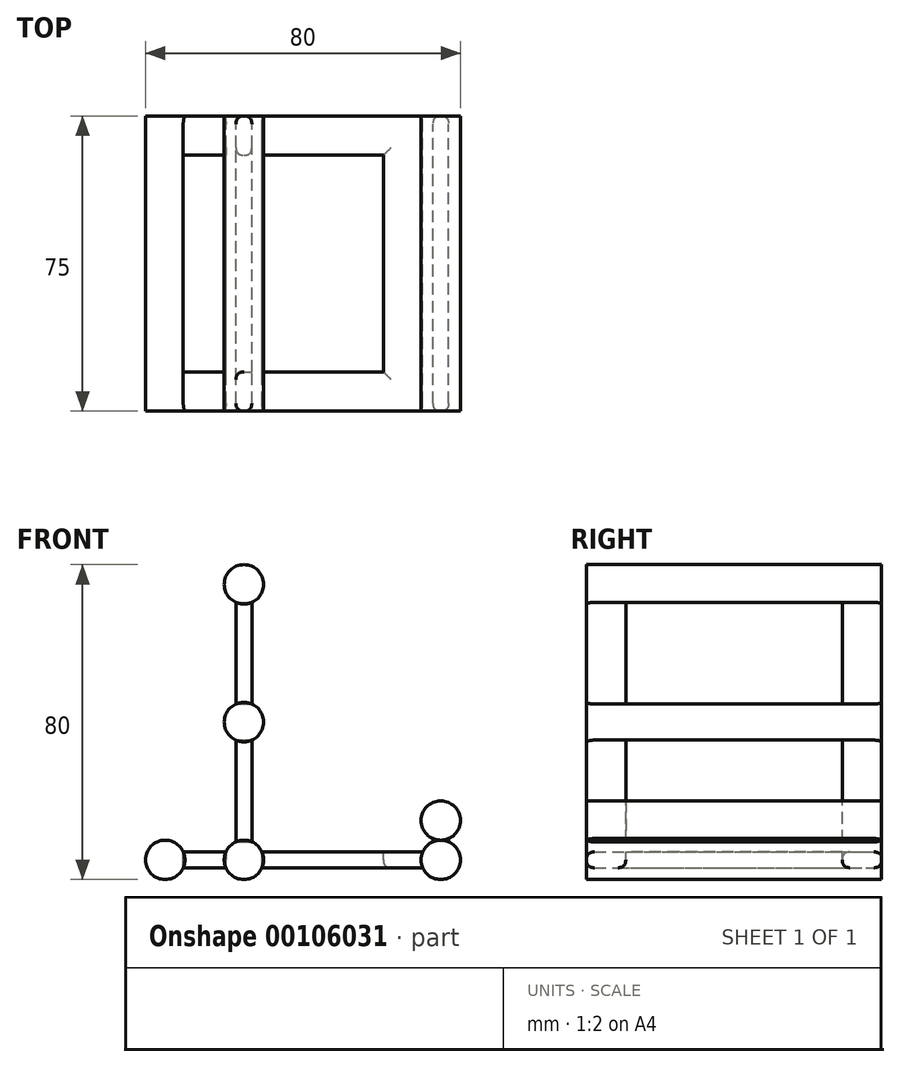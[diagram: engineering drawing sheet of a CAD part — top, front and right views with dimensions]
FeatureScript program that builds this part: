
annotation { "Feature Type Name" : "Feature", "Feature Type Description" : "" }
export const myFeature = defineFeature(function(context is Context, id is Id, definition is map)
    precondition{}
    {
        {
            var Q0;
            Q0=qCreatedBy(makeId("Front.planeOp"),FACE);
            var sketch = newSketch(context, id + "F0", { "sketchPlane" : qUnion([Q0])});
            skArc(sketch, "E0", {"start": v(3, 9.58) * mm, "mid": v(1.46, 8.54) * mm, "end": v(0.42, 7) * mm});
            skArc(sketch, "E1", {"start": v(50.42, 3) * mm, "mid": v(58.54, 1.46) * mm, "end": v(57, 9.58) * mm});
            skArc(sketch, "E2", {"start": v(7, 70.42) * mm, "mid": v(5, 80) * mm, "end": v(3, 70.42) * mm});
            skArc(sketch, "E3", {"start": v(3, 44.58) * mm, "mid": v(0, 40) * mm, "end": v(3, 35.42) * mm});
            skLineSegment(sketch, "E4.top", {"start": v(7, 5) * mm, "end": v(5, 5) * mm});
            skLineSegment(sketch, "E4.left", {"start": v(7, 70.42) * mm, "end": v(7, 44.58) * mm});
            skLineSegment(sketch, "E4.right", {"start": v(3, 70.42) * mm, "end": v(3, 44.58) * mm});
            skLineSegment(sketch, "E5.bottom", {"start": v(50.42, 7) * mm, "end": v(9.58, 7) * mm});
            skLineSegment(sketch, "E5.top", {"start": v(50.42, 3) * mm, "end": v(9.58, 3) * mm});
            skLineSegment(sketch, "E5.right", {"start": v(5, 7) * mm, "end": v(5, 5) * mm});
            skPoint(sketch, "E5.middle", {"position": v(30, 5) * mm});
            skPoint(sketch, "E6.orphan", {"position": v(7, 75) * mm});
            skPoint(sketch, "E7.orphan", {"position": v(3, 75) * mm});
            skLineSegment(sketch, "E8.trimOffspring", {"start": v(7, 35.42) * mm, "end": v(7, 9.58) * mm});
            skLineSegment(sketch, "E9.trimOffspring", {"start": v(3, 35.42) * mm, "end": v(3, 9.58) * mm});
            skArc(sketch, "E10.trimOffspring", {"start": v(7, 35.42) * mm, "mid": v(10, 40) * mm, "end": v(7, 44.58) * mm});
            skPoint(sketch, "E11.orphan", {"position": v(3, 5) * mm});
            skPoint(sketch, "E12.orphan", {"position": v(5, 3) * mm});
            skArc(sketch, "E13.trimOffspring", {"start": v(9.58, 7) * mm, "mid": v(8.54, 8.54) * mm, "end": v(7, 9.58) * mm});
            skPoint(sketch, "E5.left.start.orphan", {"position": v(55, 7) * mm});
            skPoint(sketch, "E14.orphan", {"position": v(55, 3) * mm});
            skArc(sketch, "E15", {"start": v(57, 10.42) * mm, "mid": v(55, 20) * mm, "end": v(53, 10.42) * mm});
            skLineSegment(sketch, "E16.left", {"start": v(57, 10.42) * mm, "end": v(57, 9.58) * mm});
            skLineSegment(sketch, "E16.right", {"start": v(53, 10.42) * mm, "end": v(53, 9.58) * mm});
            skPoint(sketch, "E16.middle", {"position": v(55, 10) * mm});
            skArc(sketch, "E17.trimOffspring", {"start": v(53, 9.58) * mm, "mid": v(51.46, 8.54) * mm, "end": v(50.42, 7) * mm});
            skPoint(sketch, "E18.orphan", {"position": v(57, 15) * mm});
            skPoint(sketch, "E19.orphan", {"position": v(53, 15) * mm});
            skPoint(sketch, "E20.orphan", {"position": v(53, 5) * mm});
            skPoint(sketch, "E21.orphan", {"position": v(57, 5) * mm});
            skArc(sketch, "E22", {"start": v(-10.42, 7) * mm, "mid": v(-20, 5) * mm, "end": v(-10.42, 3) * mm});
            skLineSegment(sketch, "E23", {"start": v(9.58, 7) * mm, "end": v(5, 7) * mm});
            skLineSegment(sketch, "E24", {"start": v(9.58, 3) * mm, "end": v(5, 3) * mm});
            skArc(sketch, "E25.trimOffspring", {"start": v(0.42, 3) * mm, "mid": v(5, 0) * mm, "end": v(9.58, 3) * mm});
            skLineSegment(sketch, "E26.trimOffspring", {"start": v(0.42, 7) * mm, "end": v(-10.42, 7) * mm});
            skLineSegment(sketch, "E27.trimOffspring", {"start": v(0.42, 3) * mm, "end": v(-10.42, 3) * mm});
            skSolve(sketch);
        }
        {
            var Q0;
            Q0=makeQuery(id+"F0.imprint","IMPRINT",FACE,{"disambiguationData":[TD([[makeQuery(id+"F0.imprint","IMPRINT",EDGE,{"derivedFrom":sQuery(id+"F0.wireOp",EDGE,"E0")}),1.0]])]});
            extrude(context, id + "F1", {"entities" : qUnion([Q0]), "depth" : 75 * mm});
        }
        {
            var Q0;
            Q0=makeQuery(id+"F1.opExtrude","SWEPT_FACE",FACE,{"disambiguationData":[OSD([sQuery(id+"F0.wireOp",EDGE,"E4.left")])]});
            var sketch = newSketch(context, id + "F2", { "sketchPlane" : qUnion([Q0])});
            skLineSegment(sketch, "E28.bottom", {"start": v(-65, 70.42) * mm, "end": v(-10, 70.42) * mm});
            skLineSegment(sketch, "E28.top", {"start": v(-65, 44.58) * mm, "end": v(-10, 44.58) * mm});
            skLineSegment(sketch, "E28.left", {"start": v(-65, 70.42) * mm, "end": v(-65, 44.58) * mm});
            skLineSegment(sketch, "E28.right", {"start": v(-10, 70.42) * mm, "end": v(-10, 44.58) * mm});
            skSolve(sketch);
        }
        {
            var Q0;
            Q0=makeQuery(id+"F1.opExtrude","SWEPT_FACE",FACE,{"disambiguationData":[OSD([sQuery(id+"F0.wireOp",EDGE,"E8.trimOffspring")])]});
            var sketch = newSketch(context, id + "F3", { "sketchPlane" : qUnion([Q0])});
            skLineSegment(sketch, "E29.bottom", {"start": v(-65, 35.42) * mm, "end": v(-10, 35.42) * mm});
            skLineSegment(sketch, "E29.top", {"start": v(-65, 9.58) * mm, "end": v(-10, 9.58) * mm});
            skLineSegment(sketch, "E29.left", {"start": v(-65, 35.42) * mm, "end": v(-65, 9.58) * mm});
            skLineSegment(sketch, "E29.right", {"start": v(-10, 35.42) * mm, "end": v(-10, 9.58) * mm});
            skSolve(sketch);
        }
        {
            var Q0;
            Q0=makeQuery(id+"F1.opExtrude","SWEPT_FACE",FACE,{"disambiguationData":[OSD([sQuery(id+"F0.wireOp",EDGE,"E5.bottom")])]});
            var sketch = newSketch(context, id + "F4", { "sketchPlane" : qUnion([Q0])});
            skLineSegment(sketch, "E30.bottom", {"start": v(9.58, -10) * mm, "end": v(40.42, -10) * mm});
            skLineSegment(sketch, "E30.top", {"start": v(9.58, -65) * mm, "end": v(40.42, -65) * mm});
            skLineSegment(sketch, "E30.left", {"start": v(9.58, -10) * mm, "end": v(9.58, -65) * mm});
            skLineSegment(sketch, "E30.right", {"start": v(40.42, -10) * mm, "end": v(40.42, -65) * mm});
            skSolve(sketch);
        }
        {
            var Q0;
            Q0=makeQuery(id+"F2.imprint","IMPRINT",FACE,{"disambiguationData":[TD([[makeQuery(id+"F2.imprint","IMPRINT",EDGE,{"derivedFrom":sQuery(id+"F2.wireOp",EDGE,"E28.bottom")}),-1.0]])]});
            extrude(context, id + "F5", {"entities" : qUnion([Q0]), "operationType" : NewBodyOperationType.REMOVE, "oppositeDirection" : true, "depth" : 5 * mm});
        }
        {
            var Q0;
            Q0=makeQuery(id+"F3.imprint","IMPRINT",FACE,{"disambiguationData":[TD([[makeQuery(id+"F3.imprint","IMPRINT",EDGE,{"derivedFrom":sQuery(id+"F3.wireOp",EDGE,"E29.bottom")}),-1.0]])]});
            extrude(context, id + "F6", {"entities" : qUnion([Q0]), "operationType" : NewBodyOperationType.REMOVE, "oppositeDirection" : true, "depth" : 5 * mm});
        }
        {
            var Q0;
            Q0=makeQuery(id+"F4.imprint","IMPRINT",FACE,{"disambiguationData":[TD([[makeQuery(id+"F4.imprint","IMPRINT",EDGE,{"derivedFrom":sQuery(id+"F4.wireOp",EDGE,"E30.bottom")}),-1.0]])]});
            extrude(context, id + "F7", {"entities" : qUnion([Q0]), "operationType" : NewBodyOperationType.REMOVE, "oppositeDirection" : true, "depth" : 5 * mm});
        }
        {
            var Q0;
            Q0=makeQuery(id+"F1.opExtrude","SWEPT_FACE",FACE,{"disambiguationData":[OSD([sQuery(id+"F0.wireOp",EDGE,"E26.trimOffspring")])]});
            var sketch = newSketch(context, id + "F8", { "sketchPlane" : qUnion([Q0])});
            skLineSegment(sketch, "E31.bottom", {"start": v(0.42, -10) * mm, "end": v(-10.42, -10) * mm});
            skLineSegment(sketch, "E31.top", {"start": v(0.42, -65) * mm, "end": v(-10.42, -65) * mm});
            skLineSegment(sketch, "E31.left", {"start": v(0.42, -10) * mm, "end": v(0.42, -65) * mm});
            skLineSegment(sketch, "E31.right", {"start": v(-10.42, -10) * mm, "end": v(-10.42, -65) * mm});
            skSolve(sketch);
        }
        {
            var Q0;
            Q0=makeQuery(id+"F8.imprint","IMPRINT",FACE,{"disambiguationData":[TD([[makeQuery(id+"F8.imprint","IMPRINT",EDGE,{"derivedFrom":sQuery(id+"F8.wireOp",EDGE,"E31.bottom")}),1.0]])]});
            extrude(context, id + "F9", {"entities" : qUnion([Q0]), "operationType" : NewBodyOperationType.REMOVE, "oppositeDirection" : true, "depth" : 5 * mm});
        }
        {
            var Q0;
            Q0=makeQuery(id+"F1.opExtrude","CAP_EDGE",EDGE,{"disambiguationData":[OSD([sQuery(id+"F0.wireOp",EDGE,"E27.trimOffspring")])],"isStart":false});
            var Q1;
            Q1=makeQuery(id+"F9.boolean.opBoolean","INTERSECT",EDGE,{"derivedFrom":[makeQuery(id+"F1.opExtrude","SWEPT_FACE",FACE,{"disambiguationData":[OSD([sQuery(id+"F0.wireOp",EDGE,"E27.trimOffspring")])]}),makeQuery(id+"F9.opExtrude","SWEPT_FACE",FACE,{"disambiguationData":[OSD([sQuery(id+"F8.wireOp",EDGE,"E31.bottom")])]})]});
            var Q2;
            Q2=makeQuery(id+"F1.opExtrude","CAP_EDGE",EDGE,{"disambiguationData":[OSD([sQuery(id+"F0.wireOp",EDGE,"E27.trimOffspring")])],"isStart":true});
            var Q3;
            Q3=makeQuery(id+"F1.opExtrude","CAP_EDGE",EDGE,{"disambiguationData":[OSD([sQuery(id+"F0.wireOp",EDGE,"E5.top")])],"isStart":false});
            var Q4;
            Q4=makeQuery(id+"F7.boolean.opBoolean","INTERSECT",EDGE,{"derivedFrom":[makeQuery(id+"F1.opExtrude","SWEPT_FACE",FACE,{"disambiguationData":[OSD([sQuery(id+"F0.wireOp",EDGE,"E5.top")])]}),makeQuery(id+"F7.opExtrude","SWEPT_FACE",FACE,{"disambiguationData":[OSD([sQuery(id+"F4.wireOp",EDGE,"E30.top")])]})]});
            var Q5;
            Q5=makeQuery(id+"F7.boolean.opBoolean","INTERSECT",EDGE,{"derivedFrom":[makeQuery(id+"F1.opExtrude","SWEPT_FACE",FACE,{"disambiguationData":[OSD([sQuery(id+"F0.wireOp",EDGE,"E5.top")])]}),makeQuery(id+"F7.opExtrude","SWEPT_FACE",FACE,{"disambiguationData":[OSD([sQuery(id+"F4.wireOp",EDGE,"E30.right")])]})]});
            var Q6;
            Q6=makeQuery(id+"F7.boolean.opBoolean","INTERSECT",EDGE,{"derivedFrom":[makeQuery(id+"F1.opExtrude","SWEPT_FACE",FACE,{"disambiguationData":[OSD([sQuery(id+"F0.wireOp",EDGE,"E5.top")])]}),makeQuery(id+"F7.opExtrude","SWEPT_FACE",FACE,{"disambiguationData":[OSD([sQuery(id+"F4.wireOp",EDGE,"E30.bottom")])]})]});
            var Q7;
            Q7=makeQuery(id+"F1.opExtrude","CAP_EDGE",EDGE,{"disambiguationData":[OSD([sQuery(id+"F0.wireOp",EDGE,"E5.top")])],"isStart":true});
            var Q8;
            Q8=makeQuery(id+"F9.boolean.opBoolean","INTERSECT",EDGE,{"derivedFrom":[makeQuery(id+"F1.opExtrude","SWEPT_FACE",FACE,{"disambiguationData":[OSD([sQuery(id+"F0.wireOp",EDGE,"E27.trimOffspring")])]}),makeQuery(id+"F9.opExtrude","SWEPT_FACE",FACE,{"disambiguationData":[OSD([sQuery(id+"F8.wireOp",EDGE,"E31.top")])]})]});
            var Q9;
            Q9=makeQuery(id+"F1.opExtrude","CAP_EDGE",EDGE,{"disambiguationData":[OSD([sQuery(id+"F0.wireOp",EDGE,"E26.trimOffspring")])],"isStart":false});
            var Q10;
            Q10=makeQuery(id+"F9.boolean.opBoolean","COPY",EDGE,{"derivedFrom":makeQuery(id+"F9.opExtrude","CAP_EDGE",EDGE,{"disambiguationData":[OSD([sQuery(id+"F8.wireOp",EDGE,"E31.top")])],"isStart":true})});
            var Q11;
            Q11=makeQuery(id+"F1.opExtrude","CAP_EDGE",EDGE,{"disambiguationData":[OSD([sQuery(id+"F0.wireOp",EDGE,"E5.bottom")])],"isStart":false});
            var Q12;
            Q12=makeQuery(id+"F7.boolean.opBoolean","COPY",EDGE,{"derivedFrom":makeQuery(id+"F7.opExtrude","CAP_EDGE",EDGE,{"disambiguationData":[OSD([sQuery(id+"F4.wireOp",EDGE,"E30.top")])],"isStart":true})});
            var Q13;
            Q13=makeQuery(id+"F9.boolean.opBoolean","COPY",EDGE,{"derivedFrom":makeQuery(id+"F9.opExtrude","CAP_EDGE",EDGE,{"disambiguationData":[OSD([sQuery(id+"F8.wireOp",EDGE,"E31.bottom")])],"isStart":true})});
            var Q14;
            Q14=makeQuery(id+"F7.boolean.opBoolean","COPY",EDGE,{"derivedFrom":makeQuery(id+"F7.opExtrude","CAP_EDGE",EDGE,{"disambiguationData":[OSD([sQuery(id+"F4.wireOp",EDGE,"E30.bottom")])],"isStart":true})});
            var Q15;
            Q15=makeQuery(id+"F1.opExtrude","CAP_EDGE",EDGE,{"disambiguationData":[OSD([sQuery(id+"F0.wireOp",EDGE,"E26.trimOffspring")])],"isStart":true});
            var Q16;
            Q16=makeQuery(id+"F1.opExtrude","CAP_EDGE",EDGE,{"disambiguationData":[OSD([sQuery(id+"F0.wireOp",EDGE,"E5.bottom")])],"isStart":true});
            var Q17;
            Q17=makeQuery(id+"F1.opExtrude","CAP_EDGE",EDGE,{"disambiguationData":[OSD([sQuery(id+"F0.wireOp",EDGE,"E8.trimOffspring")])],"isStart":true});
            var Q18;
            Q18=makeQuery(id+"F1.opExtrude","CAP_EDGE",EDGE,{"disambiguationData":[OSD([sQuery(id+"F0.wireOp",EDGE,"E9.trimOffspring")])],"isStart":true});
            var Q19;
            Q19=makeQuery(id+"F1.opExtrude","CAP_EDGE",EDGE,{"disambiguationData":[OSD([sQuery(id+"F0.wireOp",EDGE,"E4.right")])],"isStart":true});
            var Q20;
            Q20=makeQuery(id+"F1.opExtrude","CAP_EDGE",EDGE,{"disambiguationData":[OSD([sQuery(id+"F0.wireOp",EDGE,"E4.left")])],"isStart":true});
            var Q21;
            Q21=makeQuery(id+"F5.boolean.opBoolean","INTERSECT",EDGE,{"derivedFrom":[makeQuery(id+"F1.opExtrude","SWEPT_FACE",FACE,{"disambiguationData":[OSD([sQuery(id+"F0.wireOp",EDGE,"E4.right")])]}),makeQuery(id+"F5.opExtrude","SWEPT_FACE",FACE,{"disambiguationData":[OSD([sQuery(id+"F2.wireOp",EDGE,"E28.left")])]})]});
            var Q22;
            Q22=makeQuery(id+"F5.boolean.opBoolean","COPY",EDGE,{"derivedFrom":makeQuery(id+"F5.opExtrude","CAP_EDGE",EDGE,{"disambiguationData":[OSD([sQuery(id+"F2.wireOp",EDGE,"E28.left")])],"isStart":true})});
            var Q23;
            Q23=makeQuery(id+"F6.boolean.opBoolean","COPY",EDGE,{"derivedFrom":makeQuery(id+"F6.opExtrude","CAP_EDGE",EDGE,{"disambiguationData":[OSD([sQuery(id+"F3.wireOp",EDGE,"E29.left")])],"isStart":true})});
            var Q24;
            Q24=makeQuery(id+"F6.boolean.opBoolean","INTERSECT",EDGE,{"derivedFrom":[makeQuery(id+"F1.opExtrude","SWEPT_FACE",FACE,{"disambiguationData":[OSD([sQuery(id+"F0.wireOp",EDGE,"E9.trimOffspring")])]}),makeQuery(id+"F6.opExtrude","SWEPT_FACE",FACE,{"disambiguationData":[OSD([sQuery(id+"F3.wireOp",EDGE,"E29.left")])]})]});
            var Q25;
            Q25=makeQuery(id+"F6.boolean.opBoolean","INTERSECT",EDGE,{"derivedFrom":[makeQuery(id+"F1.opExtrude","SWEPT_FACE",FACE,{"disambiguationData":[OSD([sQuery(id+"F0.wireOp",EDGE,"E9.trimOffspring")])]}),makeQuery(id+"F6.opExtrude","SWEPT_FACE",FACE,{"disambiguationData":[OSD([sQuery(id+"F3.wireOp",EDGE,"E29.right")])]})]});
            var Q26;
            Q26=makeQuery(id+"F5.boolean.opBoolean","INTERSECT",EDGE,{"derivedFrom":[makeQuery(id+"F1.opExtrude","SWEPT_FACE",FACE,{"disambiguationData":[OSD([sQuery(id+"F0.wireOp",EDGE,"E4.right")])]}),makeQuery(id+"F5.opExtrude","SWEPT_FACE",FACE,{"disambiguationData":[OSD([sQuery(id+"F2.wireOp",EDGE,"E28.right")])]})]});
            var Q27;
            Q27=makeQuery(id+"F6.boolean.opBoolean","COPY",EDGE,{"derivedFrom":makeQuery(id+"F6.opExtrude","CAP_EDGE",EDGE,{"disambiguationData":[OSD([sQuery(id+"F3.wireOp",EDGE,"E29.right")])],"isStart":true})});
            var Q28;
            Q28=makeQuery(id+"F5.boolean.opBoolean","COPY",EDGE,{"derivedFrom":makeQuery(id+"F5.opExtrude","CAP_EDGE",EDGE,{"disambiguationData":[OSD([sQuery(id+"F2.wireOp",EDGE,"E28.right")])],"isStart":true})});
            var Q29;
            Q29=makeQuery(id+"F1.opExtrude","CAP_EDGE",EDGE,{"disambiguationData":[OSD([sQuery(id+"F0.wireOp",EDGE,"E9.trimOffspring")])],"isStart":false});
            var Q30;
            Q30=makeQuery(id+"F1.opExtrude","CAP_EDGE",EDGE,{"disambiguationData":[OSD([sQuery(id+"F0.wireOp",EDGE,"E8.trimOffspring")])],"isStart":false});
            var Q31;
            Q31=makeQuery(id+"F1.opExtrude","CAP_EDGE",EDGE,{"disambiguationData":[OSD([sQuery(id+"F0.wireOp",EDGE,"E4.left")])],"isStart":false});
            var Q32;
            Q32=makeQuery(id+"F1.opExtrude","CAP_EDGE",EDGE,{"disambiguationData":[OSD([sQuery(id+"F0.wireOp",EDGE,"E4.right")])],"isStart":false});
            var Q33;
            Q33=makeQuery(id+"F7.boolean.opBoolean","COPY",EDGE,{"derivedFrom":makeQuery(id+"F7.opExtrude","CAP_EDGE",EDGE,{"disambiguationData":[OSD([sQuery(id+"F4.wireOp",EDGE,"E30.right")])],"isStart":true})});
            var Q34;
            Q34=makeQuery(id+"F1.opExtrude","CAP_EDGE",EDGE,{"disambiguationData":[OSD([sQuery(id+"F0.wireOp",EDGE,"E16.right")])],"isStart":true});
            var Q35;
            Q35=makeQuery(id+"F1.opExtrude","CAP_EDGE",EDGE,{"disambiguationData":[OSD([sQuery(id+"F0.wireOp",EDGE,"E16.left")])],"isStart":true});
            var Q36;
            Q36=makeQuery(id+"F1.opExtrude","CAP_EDGE",EDGE,{"disambiguationData":[OSD([sQuery(id+"F0.wireOp",EDGE,"E16.right")])],"isStart":false});
            var Q37;
            Q37=makeQuery(id+"F1.opExtrude","CAP_EDGE",EDGE,{"disambiguationData":[OSD([sQuery(id+"F0.wireOp",EDGE,"E16.left")])],"isStart":false});
            fillet(context, id + "F10", {"entities" : qUnion([Q0, Q1, Q2, Q3, Q4, Q5, Q6, Q7, Q8, Q9, Q10, Q11, Q12, Q13, Q14, Q15, Q16, Q17, Q18, Q19, Q20, Q21, Q22, Q23, Q24, Q25, Q26, Q27, Q28, Q29, Q30, Q31, Q32, Q33, Q34, Q35, Q36, Q37]), "radius" : 2 * mm, "tangentPropagation" : true, "rho" : 0.5, "crossSection" : FilletCrossSection.CONIC, "allowEdgeOverflow" : false});
        }
    });
